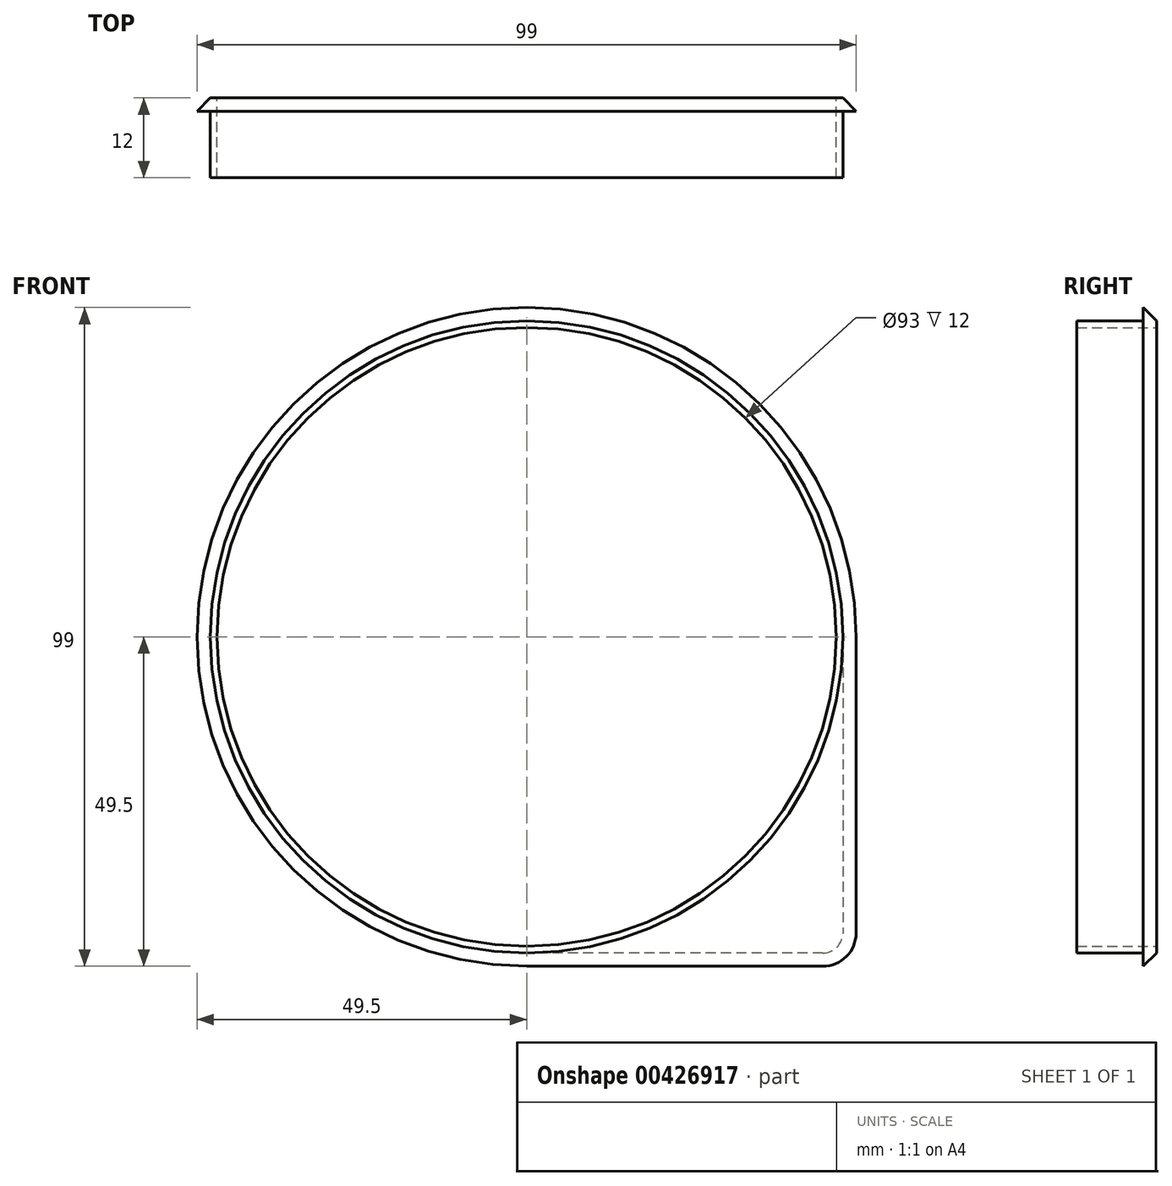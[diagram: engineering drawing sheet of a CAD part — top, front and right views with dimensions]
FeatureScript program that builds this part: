
annotation { "Feature Type Name" : "Feature", "Feature Type Description" : "" }
export const myFeature = defineFeature(function(context is Context, id is Id, definition is map)
    precondition{}
    {
        {
            var Q0;
            Q0=qCreatedBy(makeId("Front.planeOp"),FACE);
            var sketch = newSketch(context, id + "F0", { "sketchPlane" : qUnion([Q0])});
            skCircle(sketch, "E0", {"center": v(0, 0) * mm, "radius": 46.5 * mm});
            skCircle(sketch, "E1", {"center": v(0, 0) * mm, "radius": 47.5 * mm});
            skCircle(sketch, "E2", {"center": v(0, 0) * mm, "radius": 49.5 * mm});
            skLineSegment(sketch, "E3", {"start": v(0, -49.5) * mm, "end": v(44.5, -49.5) * mm});
            skLineSegment(sketch, "E4", {"start": v(49.5, -44.5) * mm, "end": v(49.5, 0) * mm});
            skPoint(sketch, "E5.visualSharp", {"position": v(49.5, -49.5) * mm});
            skArc(sketch, "E5.filletArc", {"start": v(44.5, -49.5) * mm, "mid": v(48.04, -48.04) * mm, "end": v(49.5, -44.5) * mm});
            skSolve(sketch);
        }
        {
            var Q0;
            Q0=makeQuery(id+"F0.imprint","IMPRINT",FACE,{"disambiguationData":[TD([[makeQuery(id+"F0.imprint","IMPRINT",EDGE,{"derivedFrom":sQuery(id+"F0.wireOp",EDGE,"E0")}),-1.0]])]});
            var Q1;
            Q1=makeQuery(id+"F0.imprint","IMPRINT",FACE,{"disambiguationData":[TD([[makeQuery(id+"F0.imprint","IMPRINT",EDGE,{"derivedFrom":sQuery(id+"F0.wireOp",EDGE,"E1")}),-1.0]])]});
            var Q2;
            {var subQ0=sQuery(id+"F0.wireOp",EDGE,"E3");Q2=makeQuery(id+"F0.imprint","IMPRINT",FACE,{"disambiguationData":[TD([[makeQuery(id+"F0.imprint","IMPRINT",EDGE,{"derivedFrom":subQ0}),1.0]])]});}
            extrude(context, id + "F1", {"entities" : qUnion([Q0, Q1, Q2]), "depth" : 2 * mm});
        }
        {
            var Q0;
            Q0=makeQuery(id+"F0.imprint","IMPRINT",FACE,{"disambiguationData":[TD([[makeQuery(id+"F0.imprint","IMPRINT",EDGE,{"derivedFrom":sQuery(id+"F0.wireOp",EDGE,"E0")}),-1.0]])]});
            extrude(context, id + "F2", {"entities" : qUnion([Q0]), "operationType" : NewBodyOperationType.ADD, "depth" : 12 * mm});
        }
        {
            var Q0;
            Q0=makeQuery(id+"F1.opExtrude","CAP_EDGE",EDGE,{"disambiguationData":[OSD([sQuery(id+"F0.wireOp",EDGE,"E4")])],"isStart":true});
            chamfer(context, id + "F3", {"entities" : qUnion([Q0]), "width" : 2 * mm, "tangentPropagation" : true});
        }
    });
